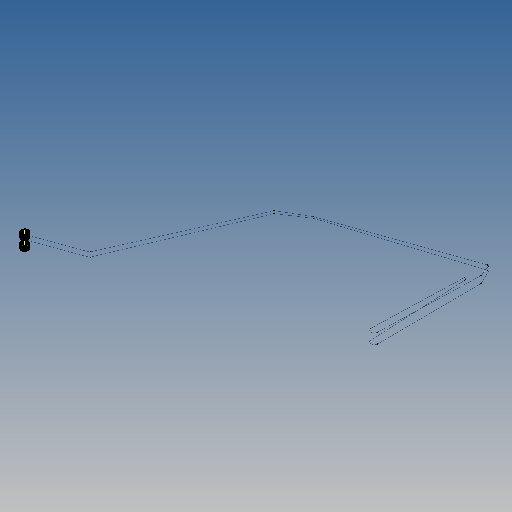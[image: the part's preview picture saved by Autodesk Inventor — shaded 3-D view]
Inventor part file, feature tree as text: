
AUTODESK INVENTOR PART (.ipt)
format: ipt  version: 2025 (Build 290162010, 162A)  size: 730,112 bytes
history: native  units: mm
features: sketch x18, other x17, plane x14, sweep x7, loft x7, mirror x1
ambient origin geometry x8: Origin, YZ Plane, XZ Plane, XY Plane, X Axis, Y Axis, Z Axis, Center Point
bodies: Volumenkörper1 (feature_tree)
feature tree (64):
  sketch  "Skizze1"  dims[d0=25.0mm d1=73.469mm]
  plane  "Arbeitsebene1"
  sketch  "Skizze2"  dims[d2=153.659mm d3=8.0mm]
  plane  "Arbeitsebene2"
  sweep  "Sweeping1"
  other  "Spirale1"
  plane  "Arbeitsebene3"
  other  "Spirale2"
  loft  "Erhebung1"
  plane  "Arbeitsebene4"
  other  "Spirale3"
  loft  "Erhebung2"
  plane  "Arbeitsebene5"
  sketch  "Skizze7"  dims[d12=913.524mm d13=894.428mm]
  plane  "Arbeitsebene6"
  sweep  "Sweeping2"
  loft  "Erhebung3"
  plane  "Arbeitsebene7"
  sketch  "Skizze9"  dims[d16=887.348mm d17=650.951mm]
  plane  "Arbeitsebene8"
  sweep  "Sweeping3"
  loft  "Erhebung4"
  sketch  "Skizze11"  dims[d20=15.338mm d21=0.5mm]
  plane  "Arbeitsebene9"
  sweep  "Sweeping4"
  loft  "Erhebung5"
  plane  "Arbeitsebene10"
  sketch  "Skizze13"  dims[d24=0.0mm d25=0.0mm]
  plane  "Arbeitsebene11"
  sweep  "Sweeping5"
  loft  "Erhebung6"
  plane  "Arbeitsebene12"
  sketch  "Skizze15"  dims[d35=1.0mm d36=11.5mm]
  plane  "Arbeitsebene13"
  sweep  "Sweeping6"
  loft  "Erhebung7"
  sketch  "Skizze17"  dims[d45=10.0mm d46=90.0deg]
  plane  "Arbeitsebene14"
  sweep  "Sweeping7"
  mirror  "Spiegeln1"
  sketch  "Skizze3"  dims[d4=0.5mm d5=518.929mm]
  sketch  "Skizze4"  dims[d6=355.121mm d7=8.0mm]
  sketch  "Skizze5"  dims[d8=570.581mm d9=438.329mm]
  other  "Kanten1"
  other  "Kanten2"
  sketch  "Skizze6"  dims[d10=723.059mm d11=679.021mm]
  other  "Kanten3"
  other  "Kanten4"
  sketch  "Skizze8"  dims[d14=22.4mm d15=320.8mm]
  other  "Kanten5"
  other  "Kanten6"
  sketch  "Skizze10"  dims[d18=8.0mm d19=30.676mm]
  other  "Kanten7"
  other  "Kanten8"
  sketch  "Skizze12"  dims[d22=8.0mm d23=1.0mm]
  other  "Kanten9"
  other  "Kanten10"
  sketch  "Skizze14"  dims[d26=1.001mm d27=17.4mm d28=2.5mm d29=0.0mm d30=90.0deg d31=90.0deg d32=0.0mm d33=0.0mm d34=90.0deg]
  other  "Kanten11"
  other  "Kanten12"
  sketch  "Skizze16"  dims[d37=1.001mm d38=18.8mm d39=2.5mm d40=0.0mm d41=90.0deg d42=90.0deg d43=0.0mm d44=0.0mm]
  other  "Kanten13"
  other  "Kanten14"
  sketch  "Skizze18"  dims[d47=12.5mm d48=90.0deg d49=90.0deg d50=1.0mm d51=10.5mm d52=1.001mm d53=18.8mm d54=2.5mm d55=0.0mm d56=90.0deg d57=90.0deg d58=0.0mm d59=0.0mm d60=10.0mm d61=90.0deg d62=12.5mm d63=90.0deg d64=4.5mm d65=1.0mm d66=0.0mm d67=0.0mm d68=0.0mm d69=90.0deg d70=0.0mm d71=90.0deg d72=2.5mm d73=1.0mm d74=0.0mm d75=0.0mm d76=0.0mm d77=90.0deg d78=0.0mm d79=90.0deg d80=1.0mm d81=0.0mm d82=0.0mm d83=0.0mm d84=90.0deg d85=0.0mm d86=90.0deg d87=12.0mm d88=1.0mm d89=0.0mm d90=0.0mm d91=0.0mm d92=90.0deg d93=0.0mm d94=90.0deg d95=18.0mm d96=1.0mm d97=0.0mm d98=0.0mm d99=0.0mm d100=90.0deg d101=0.0mm d102=90.0deg d103=90.0deg d104=8.0mm d105=0.5mm d106=0.0mm d107=0.0mm]
